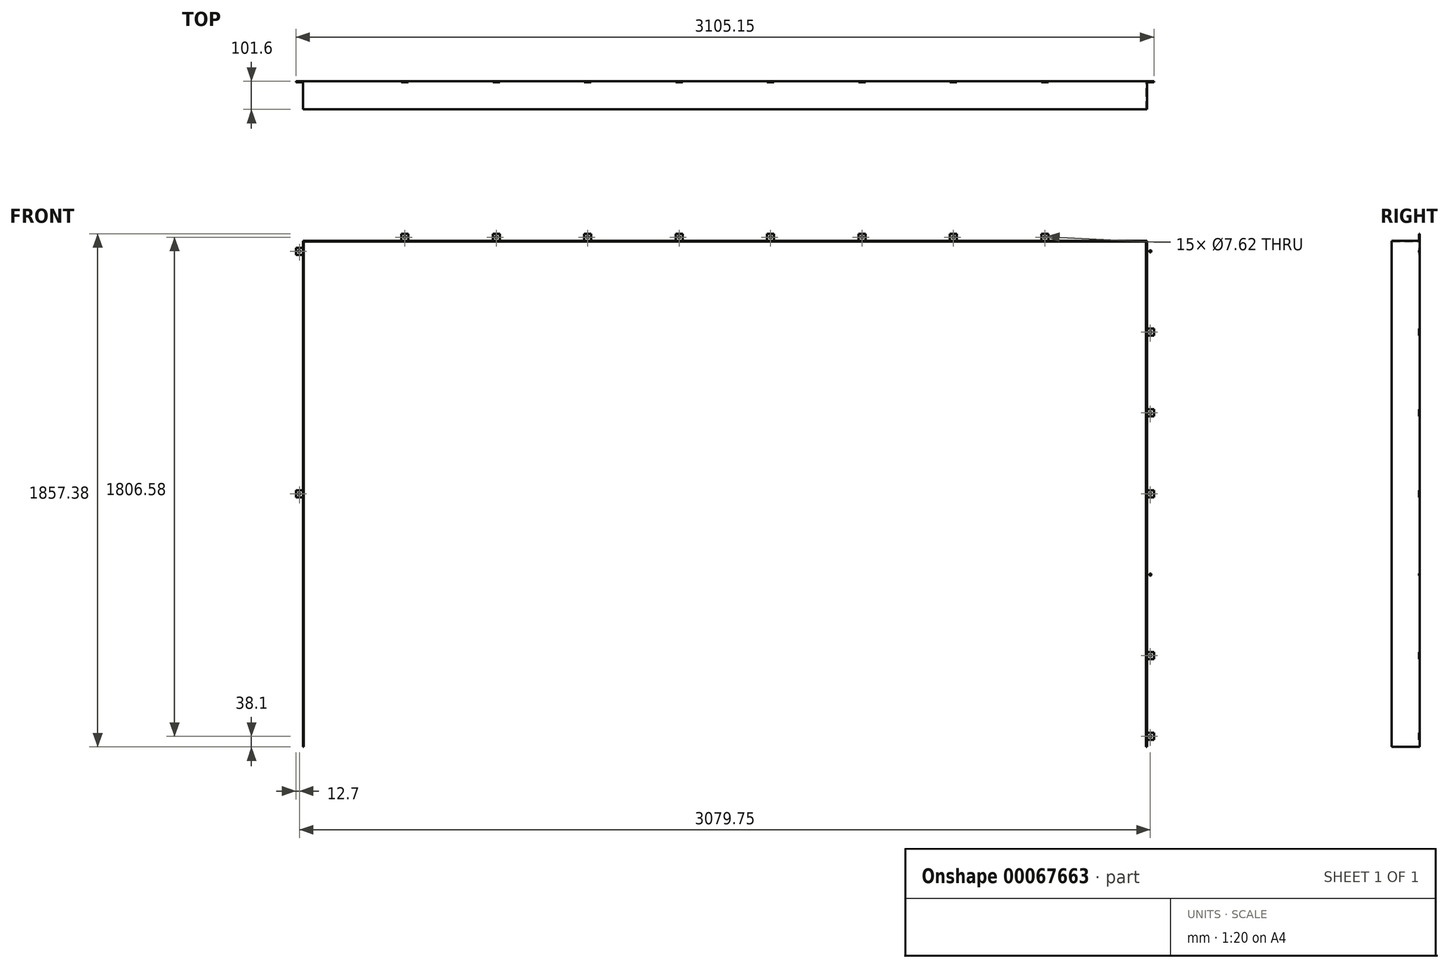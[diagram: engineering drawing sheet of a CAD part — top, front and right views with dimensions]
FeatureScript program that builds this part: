
annotation { "Feature Type Name" : "Feature", "Feature Type Description" : "" }
export const myFeature = defineFeature(function(context is Context, id is Id, definition is map)
    precondition{}
    {
        {
            var Q0;
            Q0=qCreatedBy(makeId("Front.planeOp"),FACE);
            var sketch = newSketch(context, id + "F0", { "sketchPlane" : qUnion([Q0])});
            skLineSegment(sketch, "E0", {"start": v(0, 0) * mm, "end": v(0, 1831.98) * mm});
            skLineSegment(sketch, "E1", {"start": v(0, 1831.98) * mm, "end": v(3054.35, 1831.98) * mm});
            skLineSegment(sketch, "E2", {"start": v(3054.35, 1831.98) * mm, "end": v(3054.35, 0) * mm});
            skLineSegment(sketch, "E3", {"start": v(3054.35, 0) * mm, "end": v(3051.18, 0) * mm});
            skLineSegment(sketch, "E4", {"start": v(3051.18, 0) * mm, "end": v(3051.18, 1828.8) * mm});
            skLineSegment(sketch, "E5", {"start": v(3051.18, 1828.8) * mm, "end": v(3.17, 1828.8) * mm});
            skLineSegment(sketch, "E6", {"start": v(3.18, 1828.8) * mm, "end": v(3.18, 0) * mm});
            skLineSegment(sketch, "E7", {"start": v(3.18, 0) * mm, "end": v(0, 0) * mm});
            skLineSegment(sketch, "E8", {"start": v(1527.18, 1831.98) * mm, "end": v(1527.18, 1828.8) * mm, "construction": true});
            skLineSegment(sketch, "E9", {"start": v(1527.18, 1828.8) * mm, "end": v(1527.18, -376.43) * mm, "construction": true});
            skLineSegment(sketch, "E10.bottom", {"start": v(0, 1806.57) * mm, "end": v(-25.4, 1806.57) * mm});
            skLineSegment(sketch, "E10.top", {"start": v(0, 1781.17) * mm, "end": v(-25.4, 1781.17) * mm});
            skLineSegment(sketch, "E10.left", {"start": v(0, 1806.57) * mm, "end": v(0, 1781.17) * mm});
            skLineSegment(sketch, "E10.right", {"start": v(-25.4, 1806.57) * mm, "end": v(-25.4, 1781.17) * mm});
            skLineSegment(sketch, "E11", {"start": v(-12.7, 1806.57) * mm, "end": v(-12.7, 1781.17) * mm, "construction": true});
            skLineSegment(sketch, "E12", {"start": v(-25.4, 1793.87) * mm, "end": v(0, 1793.87) * mm, "construction": true});
            skCircle(sketch, "E13", {"center": v(-12.7, 1793.87) * mm, "radius": 3.81 * mm});
            skLineSegment(sketch, "E14.left", {"start": v(0, 1513.95) * mm, "end": v(0, 1488.55) * mm});
            skLineSegment(sketch, "E15", {"start": v(-25.4, 1501.25) * mm, "end": v(0, 1501.25) * mm, "construction": true});
            skLineSegment(sketch, "E16", {"start": v(-12.7, 1513.95) * mm, "end": v(-12.7, 1488.55) * mm, "construction": true});
            skLineSegment(sketch, "E14.right", {"start": v(-25.4, 1513.95) * mm, "end": v(-25.4, 1488.55) * mm});
            skLineSegment(sketch, "E14.top", {"start": v(0, 1488.55) * mm, "end": v(-25.4, 1488.55) * mm});
            skLineSegment(sketch, "E14.bottom", {"start": v(0, 1513.95) * mm, "end": v(-25.4, 1513.95) * mm});
            skCircle(sketch, "E17", {"center": v(-12.7, 1501.25) * mm, "radius": 3.81 * mm});
            skLineSegment(sketch, "E18.left", {"start": v(0, 1221.32) * mm, "end": v(0, 1195.92) * mm});
            skLineSegment(sketch, "E19", {"start": v(-25.4, 1208.62) * mm, "end": v(0, 1208.62) * mm, "construction": true});
            skLineSegment(sketch, "E20", {"start": v(-12.7, 1221.32) * mm, "end": v(-12.7, 1195.92) * mm, "construction": true});
            skLineSegment(sketch, "E18.right", {"start": v(-25.4, 1221.32) * mm, "end": v(-25.4, 1195.92) * mm});
            skLineSegment(sketch, "E18.top", {"start": v(0, 1195.92) * mm, "end": v(-25.4, 1195.92) * mm});
            skLineSegment(sketch, "E18.bottom", {"start": v(0, 1221.32) * mm, "end": v(-25.4, 1221.32) * mm});
            skCircle(sketch, "E21", {"center": v(-12.7, 1208.62) * mm, "radius": 3.81 * mm});
            skLineSegment(sketch, "E22.left", {"start": v(0, 50.8) * mm, "end": v(0, 25.4) * mm});
            skLineSegment(sketch, "E23", {"start": v(-25.4, 38.1) * mm, "end": v(0, 38.1) * mm, "construction": true});
            skLineSegment(sketch, "E24", {"start": v(-12.7, 50.8) * mm, "end": v(-12.7, 25.4) * mm, "construction": true});
            skLineSegment(sketch, "E22.right", {"start": v(-25.4, 50.8) * mm, "end": v(-25.4, 25.4) * mm});
            skLineSegment(sketch, "E22.top", {"start": v(0, 25.4) * mm, "end": v(-25.4, 25.4) * mm});
            skLineSegment(sketch, "E22.bottom", {"start": v(0, 50.8) * mm, "end": v(-25.4, 50.8) * mm});
            skCircle(sketch, "E25", {"center": v(-12.7, 38.1) * mm, "radius": 3.81 * mm});
            skLineSegment(sketch, "E26.left", {"start": v(0, 343.43) * mm, "end": v(0, 318.03) * mm});
            skLineSegment(sketch, "E27", {"start": v(-25.4, 330.73) * mm, "end": v(0, 330.73) * mm, "construction": true});
            skLineSegment(sketch, "E28", {"start": v(-12.7, 343.43) * mm, "end": v(-12.7, 318.03) * mm, "construction": true});
            skLineSegment(sketch, "E26.right", {"start": v(-25.4, 343.43) * mm, "end": v(-25.4, 318.03) * mm});
            skLineSegment(sketch, "E26.top", {"start": v(0, 318.03) * mm, "end": v(-25.4, 318.03) * mm});
            skLineSegment(sketch, "E26.bottom", {"start": v(0, 343.43) * mm, "end": v(-25.4, 343.43) * mm});
            skCircle(sketch, "E29", {"center": v(-12.7, 330.73) * mm, "radius": 3.81 * mm});
            skLineSegment(sketch, "E30.left", {"start": v(0, 636.06) * mm, "end": v(0, 610.66) * mm});
            skLineSegment(sketch, "E31", {"start": v(-25.4, 623.36) * mm, "end": v(0, 623.36) * mm, "construction": true});
            skLineSegment(sketch, "E32", {"start": v(-12.7, 636.06) * mm, "end": v(-12.7, 610.66) * mm, "construction": true});
            skLineSegment(sketch, "E30.right", {"start": v(-25.4, 636.06) * mm, "end": v(-25.4, 610.66) * mm});
            skLineSegment(sketch, "E30.top", {"start": v(0, 610.66) * mm, "end": v(-25.4, 610.66) * mm});
            skLineSegment(sketch, "E30.bottom", {"start": v(0, 636.06) * mm, "end": v(-25.4, 636.06) * mm});
            skCircle(sketch, "E33", {"center": v(-12.7, 623.36) * mm, "radius": 3.81 * mm});
            skLineSegment(sketch, "E34.MirrorCS", {"start": v(3079.75, 1793.87) * mm, "end": v(3054.35, 1793.87) * mm, "construction": true});
            skCircle(sketch, "E35.MirrorC", {"center": v(3067.05, 1793.88) * mm, "radius": 3.81 * mm});
            skLineSegment(sketch, "E36.MirrorCS", {"start": v(3054.35, 1806.57) * mm, "end": v(3079.75, 1806.57) * mm});
            skLineSegment(sketch, "E37.MirrorCS", {"start": v(3067.05, 1806.58) * mm, "end": v(3067.05, 1781.18) * mm, "construction": true});
            skLineSegment(sketch, "E38.MirrorCS", {"start": v(3079.75, 1806.58) * mm, "end": v(3079.75, 1781.18) * mm});
            skLineSegment(sketch, "E39.MirrorCS", {"start": v(3054.35, 1806.58) * mm, "end": v(3054.35, 1781.18) * mm});
            skLineSegment(sketch, "E40.MirrorCS", {"start": v(3054.35, 1781.17) * mm, "end": v(3079.75, 1781.17) * mm});
            skLineSegment(sketch, "E41.MirrorCS", {"start": v(3079.75, 1501.25) * mm, "end": v(3054.35, 1501.25) * mm, "construction": true});
            skLineSegment(sketch, "E42.MirrorCS", {"start": v(3054.35, 1513.95) * mm, "end": v(3079.75, 1513.95) * mm});
            skCircle(sketch, "E43.MirrorC", {"center": v(3067.05, 1501.25) * mm, "radius": 3.81 * mm});
            skLineSegment(sketch, "E44.MirrorCS", {"start": v(3054.35, 1513.95) * mm, "end": v(3054.35, 1488.55) * mm});
            skLineSegment(sketch, "E45.MirrorCS", {"start": v(3067.05, 1513.95) * mm, "end": v(3067.05, 1488.55) * mm, "construction": true});
            skLineSegment(sketch, "E46.MirrorCS", {"start": v(3079.75, 1513.95) * mm, "end": v(3079.75, 1488.55) * mm});
            skLineSegment(sketch, "E47.MirrorCS", {"start": v(3054.35, 1488.55) * mm, "end": v(3079.75, 1488.55) * mm});
            skLineSegment(sketch, "E48.MirrorCS", {"start": v(3079.75, 1221.32) * mm, "end": v(3079.75, 1195.92) * mm});
            skLineSegment(sketch, "E49.MirrorCS", {"start": v(3079.75, 1208.62) * mm, "end": v(3054.35, 1208.62) * mm, "construction": true});
            skLineSegment(sketch, "E50.MirrorCS", {"start": v(3067.05, 1221.32) * mm, "end": v(3067.05, 1195.92) * mm, "construction": true});
            skCircle(sketch, "E51.MirrorC", {"center": v(3067.05, 1208.62) * mm, "radius": 3.81 * mm});
            skLineSegment(sketch, "E52.MirrorCS", {"start": v(3054.35, 1195.92) * mm, "end": v(3079.75, 1195.92) * mm});
            skLineSegment(sketch, "E53.MirrorCS", {"start": v(3054.35, 1221.32) * mm, "end": v(3054.35, 1195.92) * mm});
            skLineSegment(sketch, "E54.MirrorCS", {"start": v(3054.35, 1221.32) * mm, "end": v(3079.75, 1221.32) * mm});
            skCircle(sketch, "E55.MirrorC", {"center": v(3067.05, 623.36) * mm, "radius": 3.81 * mm});
            skLineSegment(sketch, "E56.MirrorCS", {"start": v(3054.35, 636.06) * mm, "end": v(3079.75, 636.06) * mm});
            skLineSegment(sketch, "E57.MirrorCS", {"start": v(3079.75, 623.36) * mm, "end": v(3054.35, 623.36) * mm, "construction": true});
            skLineSegment(sketch, "E58.MirrorCS", {"start": v(3067.05, 636.06) * mm, "end": v(3067.05, 610.66) * mm, "construction": true});
            skLineSegment(sketch, "E59.MirrorCS", {"start": v(3054.35, 636.06) * mm, "end": v(3054.35, 610.66) * mm});
            skLineSegment(sketch, "E60.MirrorCS", {"start": v(3054.35, 610.66) * mm, "end": v(3079.75, 610.66) * mm});
            skLineSegment(sketch, "E61.MirrorCS", {"start": v(3079.75, 636.06) * mm, "end": v(3079.75, 610.66) * mm});
            skLineSegment(sketch, "E62.MirrorCS", {"start": v(3079.75, 343.43) * mm, "end": v(3079.75, 318.03) * mm});
            skLineSegment(sketch, "E63.MirrorCS", {"start": v(3054.35, 318.03) * mm, "end": v(3079.75, 318.03) * mm});
            skLineSegment(sketch, "E64.MirrorCS", {"start": v(3067.05, 343.43) * mm, "end": v(3067.05, 318.03) * mm, "construction": true});
            skLineSegment(sketch, "E65.MirrorCS", {"start": v(3054.35, 343.43) * mm, "end": v(3079.75, 343.43) * mm});
            skLineSegment(sketch, "E66.MirrorCS", {"start": v(3079.75, 330.73) * mm, "end": v(3054.35, 330.73) * mm, "construction": true});
            skLineSegment(sketch, "E67.MirrorCS", {"start": v(3054.35, 343.43) * mm, "end": v(3054.35, 318.03) * mm});
            skCircle(sketch, "E68.MirrorC", {"center": v(3067.05, 330.73) * mm, "radius": 3.81 * mm});
            skLineSegment(sketch, "E69.MirrorCS", {"start": v(3079.75, 50.8) * mm, "end": v(3079.75, 25.4) * mm});
            skLineSegment(sketch, "E70.MirrorCS", {"start": v(3067.05, 50.8) * mm, "end": v(3067.05, 25.4) * mm, "construction": true});
            skLineSegment(sketch, "E71.MirrorCS", {"start": v(3079.75, 38.1) * mm, "end": v(3054.35, 38.1) * mm, "construction": true});
            skCircle(sketch, "E72.MirrorC", {"center": v(3067.05, 38.1) * mm, "radius": 3.81 * mm});
            skLineSegment(sketch, "E73.MirrorCS", {"start": v(3054.35, 50.8) * mm, "end": v(3079.75, 50.8) * mm});
            skLineSegment(sketch, "E74.MirrorCS", {"start": v(3054.35, 50.8) * mm, "end": v(3054.35, 25.4) * mm});
            skLineSegment(sketch, "E75.MirrorCS", {"start": v(3054.35, 25.4) * mm, "end": v(3079.75, 25.4) * mm});
            skLineSegment(sketch, "E76.bottom", {"start": v(25.4, 1831.98) * mm, "end": v(50.8, 1831.98) * mm});
            skLineSegment(sketch, "E76.top", {"start": v(25.4, 1857.38) * mm, "end": v(50.8, 1857.38) * mm});
            skLineSegment(sketch, "E76.left", {"start": v(25.4, 1831.98) * mm, "end": v(25.4, 1857.38) * mm});
            skLineSegment(sketch, "E76.right", {"start": v(50.8, 1831.98) * mm, "end": v(50.8, 1857.38) * mm});
            skLineSegment(sketch, "E77.bottom", {"start": v(3028.95, 1831.98) * mm, "end": v(3003.55, 1831.98) * mm});
            skLineSegment(sketch, "E77.top", {"start": v(3028.95, 1857.38) * mm, "end": v(3003.55, 1857.38) * mm});
            skLineSegment(sketch, "E77.left", {"start": v(3028.95, 1831.98) * mm, "end": v(3028.95, 1857.38) * mm});
            skLineSegment(sketch, "E77.right", {"start": v(3003.55, 1831.98) * mm, "end": v(3003.55, 1857.38) * mm});
            skLineSegment(sketch, "E78", {"start": v(3003.55, 1857.38) * mm, "end": v(3028.95, 1831.97) * mm, "construction": true});
            skLineSegment(sketch, "E79", {"start": v(3028.95, 1857.37) * mm, "end": v(3003.55, 1831.97) * mm, "construction": true});
            skCircle(sketch, "E80", {"center": v(3016.25, 1844.68) * mm, "radius": 3.81 * mm});
            skLineSegment(sketch, "E81", {"start": v(25.4, 1857.38) * mm, "end": v(50.8, 1831.98) * mm, "construction": true});
            skLineSegment(sketch, "E82", {"start": v(50.8, 1857.38) * mm, "end": v(25.4, 1831.98) * mm, "construction": true});
            skCircle(sketch, "E83", {"center": v(38.1, 1844.68) * mm, "radius": 3.81 * mm});
            skLineSegment(sketch, "E84", {"start": v(356.3, 1844.68) * mm, "end": v(381.7, 1844.68) * mm, "construction": true});
            skCircle(sketch, "E85", {"center": v(369, 1844.68) * mm, "radius": 3.81 * mm});
            skLineSegment(sketch, "E86.left", {"start": v(381.7, 1857.38) * mm, "end": v(381.7, 1831.98) * mm});
            skLineSegment(sketch, "E86.top", {"start": v(381.7, 1831.98) * mm, "end": v(356.3, 1831.98) * mm});
            skLineSegment(sketch, "E86.bottom", {"start": v(381.7, 1857.38) * mm, "end": v(356.3, 1857.38) * mm});
            skLineSegment(sketch, "E87", {"start": v(369, 1857.38) * mm, "end": v(369, 1831.98) * mm, "construction": true});
            skLineSegment(sketch, "E86.right", {"start": v(356.3, 1857.38) * mm, "end": v(356.3, 1831.97) * mm});
            skLineSegment(sketch, "E88", {"start": v(1349.02, 1844.68) * mm, "end": v(1374.42, 1844.68) * mm, "construction": true});
            skCircle(sketch, "E89", {"center": v(1361.72, 1844.68) * mm, "radius": 3.81 * mm});
            skLineSegment(sketch, "E90.left", {"start": v(1374.42, 1857.38) * mm, "end": v(1374.42, 1831.98) * mm});
            skLineSegment(sketch, "E90.top", {"start": v(1374.42, 1831.98) * mm, "end": v(1349.02, 1831.98) * mm});
            skLineSegment(sketch, "E90.bottom", {"start": v(1374.42, 1857.38) * mm, "end": v(1349.02, 1857.38) * mm});
            skLineSegment(sketch, "E91", {"start": v(1361.72, 1857.38) * mm, "end": v(1361.72, 1831.98) * mm, "construction": true});
            skLineSegment(sketch, "E90.right", {"start": v(1349.02, 1857.38) * mm, "end": v(1349.02, 1831.98) * mm});
            skLineSegment(sketch, "E92", {"start": v(2341.74, 1844.68) * mm, "end": v(2367.14, 1844.68) * mm, "construction": true});
            skCircle(sketch, "E93", {"center": v(2354.44, 1844.68) * mm, "radius": 3.81 * mm});
            skLineSegment(sketch, "E94.left", {"start": v(2367.14, 1857.38) * mm, "end": v(2367.14, 1831.98) * mm});
            skLineSegment(sketch, "E94.top", {"start": v(2367.14, 1831.98) * mm, "end": v(2341.74, 1831.98) * mm});
            skLineSegment(sketch, "E94.bottom", {"start": v(2367.14, 1857.38) * mm, "end": v(2341.74, 1857.38) * mm});
            skLineSegment(sketch, "E95", {"start": v(2354.44, 1857.38) * mm, "end": v(2354.44, 1831.98) * mm, "construction": true});
            skLineSegment(sketch, "E94.right", {"start": v(2341.74, 1857.38) * mm, "end": v(2341.74, 1831.97) * mm});
            skLineSegment(sketch, "E96.top", {"start": v(0, 903.29) * mm, "end": v(-25.4, 903.29) * mm});
            skLineSegment(sketch, "E97", {"start": v(-12.7, 928.69) * mm, "end": v(-12.7, 903.29) * mm, "construction": true});
            skCircle(sketch, "E98", {"center": v(-12.7, 915.99) * mm, "radius": 3.81 * mm});
            skLineSegment(sketch, "E99", {"start": v(-25.4, 915.99) * mm, "end": v(0, 915.99) * mm, "construction": true});
            skLineSegment(sketch, "E96.left", {"start": v(0, 928.69) * mm, "end": v(0, 903.29) * mm});
            skLineSegment(sketch, "E96.bottom", {"start": v(0, 928.69) * mm, "end": v(-25.4, 928.69) * mm});
            skLineSegment(sketch, "E96.right", {"start": v(-25.4, 928.69) * mm, "end": v(-25.4, 903.29) * mm});
            skLineSegment(sketch, "E100", {"start": v(-12.7, 38.1) * mm, "end": v(-12.7, 330.73) * mm, "construction": true});
            skLineSegment(sketch, "E101", {"start": v(-12.7, 330.73) * mm, "end": v(-12.7, 623.36) * mm, "construction": true});
            skLineSegment(sketch, "E102", {"start": v(-12.7, 623.36) * mm, "end": v(-12.7, 915.99) * mm, "construction": true});
            skLineSegment(sketch, "E103", {"start": v(-12.7, 915.99) * mm, "end": v(-12.7, 1208.62) * mm, "construction": true});
            skLineSegment(sketch, "E104", {"start": v(-12.7, 1208.62) * mm, "end": v(-12.7, 1501.25) * mm, "construction": true});
            skLineSegment(sketch, "E105", {"start": v(-12.7, 1793.87) * mm, "end": v(-12.7, 1501.25) * mm, "construction": true});
            skLineSegment(sketch, "E106.MirrorCS", {"start": v(3067.05, 928.69) * mm, "end": v(3067.05, 903.29) * mm, "construction": true});
            skLineSegment(sketch, "E107.MirrorCS", {"start": v(3079.75, 915.99) * mm, "end": v(3054.35, 915.99) * mm, "construction": true});
            skLineSegment(sketch, "E108.MirrorCS", {"start": v(3054.35, 928.69) * mm, "end": v(3079.75, 928.69) * mm});
            skCircle(sketch, "E109.MirrorC", {"center": v(3067.05, 915.99) * mm, "radius": 3.81 * mm});
            skLineSegment(sketch, "E110.MirrorCS", {"start": v(3054.35, 903.29) * mm, "end": v(3079.75, 903.29) * mm});
            skLineSegment(sketch, "E111.MirrorCS", {"start": v(3079.75, 928.69) * mm, "end": v(3079.75, 903.29) * mm});
            skLineSegment(sketch, "E112.MirrorCS", {"start": v(3054.35, 928.69) * mm, "end": v(3054.35, 903.29) * mm});
            skLineSegment(sketch, "E113.left", {"start": v(1043.52, 1857.38) * mm, "end": v(1043.52, 1831.98) * mm});
            skLineSegment(sketch, "E113.top", {"start": v(1043.52, 1831.98) * mm, "end": v(1018.12, 1831.98) * mm});
            skLineSegment(sketch, "E114", {"start": v(1030.82, 1857.38) * mm, "end": v(1030.82, 1831.98) * mm, "construction": true});
            skCircle(sketch, "E115", {"center": v(1030.82, 1844.68) * mm, "radius": 3.81 * mm});
            skLineSegment(sketch, "E113.bottom", {"start": v(1043.52, 1857.38) * mm, "end": v(1018.12, 1857.38) * mm});
            skLineSegment(sketch, "E116", {"start": v(1018.12, 1844.67) * mm, "end": v(1043.52, 1844.67) * mm, "construction": true});
            skLineSegment(sketch, "E113.right", {"start": v(1018.12, 1857.38) * mm, "end": v(1018.12, 1831.98) * mm});
            skLineSegment(sketch, "E117.left", {"start": v(2036.23, 1857.38) * mm, "end": v(2036.23, 1831.98) * mm});
            skLineSegment(sketch, "E117.top", {"start": v(2036.23, 1831.98) * mm, "end": v(2010.83, 1831.98) * mm});
            skLineSegment(sketch, "E118", {"start": v(2023.53, 1857.38) * mm, "end": v(2023.53, 1831.98) * mm, "construction": true});
            skCircle(sketch, "E119", {"center": v(2023.53, 1844.68) * mm, "radius": 3.81 * mm});
            skLineSegment(sketch, "E117.bottom", {"start": v(2036.23, 1857.38) * mm, "end": v(2010.83, 1857.38) * mm});
            skLineSegment(sketch, "E120", {"start": v(2010.83, 1844.68) * mm, "end": v(2036.23, 1844.68) * mm, "construction": true});
            skLineSegment(sketch, "E117.right", {"start": v(2010.83, 1857.38) * mm, "end": v(2010.83, 1831.98) * mm});
            skLineSegment(sketch, "E121.left", {"start": v(712.61, 1857.38) * mm, "end": v(712.61, 1831.98) * mm});
            skLineSegment(sketch, "E121.top", {"start": v(712.61, 1831.98) * mm, "end": v(687.21, 1831.98) * mm});
            skLineSegment(sketch, "E122", {"start": v(699.91, 1857.38) * mm, "end": v(699.91, 1831.98) * mm, "construction": true});
            skCircle(sketch, "E123", {"center": v(699.91, 1844.68) * mm, "radius": 3.81 * mm});
            skLineSegment(sketch, "E121.bottom", {"start": v(712.61, 1857.38) * mm, "end": v(687.21, 1857.38) * mm});
            skLineSegment(sketch, "E124", {"start": v(687.21, 1844.68) * mm, "end": v(712.61, 1844.68) * mm, "construction": true});
            skLineSegment(sketch, "E121.right", {"start": v(687.21, 1857.38) * mm, "end": v(687.21, 1831.98) * mm});
            skLineSegment(sketch, "E125.left", {"start": v(2698.04, 1857.38) * mm, "end": v(2698.04, 1831.98) * mm});
            skLineSegment(sketch, "E125.top", {"start": v(2698.04, 1831.98) * mm, "end": v(2672.64, 1831.98) * mm});
            skLineSegment(sketch, "E126", {"start": v(2685.34, 1857.38) * mm, "end": v(2685.34, 1831.98) * mm, "construction": true});
            skCircle(sketch, "E127", {"center": v(2685.34, 1844.68) * mm, "radius": 3.81 * mm});
            skLineSegment(sketch, "E125.bottom", {"start": v(2698.04, 1857.38) * mm, "end": v(2672.64, 1857.38) * mm});
            skLineSegment(sketch, "E128", {"start": v(2672.64, 1844.68) * mm, "end": v(2698.04, 1844.68) * mm, "construction": true});
            skLineSegment(sketch, "E125.right", {"start": v(2672.64, 1857.38) * mm, "end": v(2672.64, 1831.98) * mm});
            skLineSegment(sketch, "E129.left", {"start": v(1705.33, 1857.38) * mm, "end": v(1705.33, 1831.98) * mm});
            skLineSegment(sketch, "E129.top", {"start": v(1705.33, 1831.97) * mm, "end": v(1679.93, 1831.97) * mm});
            skLineSegment(sketch, "E130", {"start": v(1692.63, 1857.38) * mm, "end": v(1692.63, 1831.98) * mm, "construction": true});
            skCircle(sketch, "E131", {"center": v(1692.63, 1844.68) * mm, "radius": 3.81 * mm});
            skLineSegment(sketch, "E129.bottom", {"start": v(1705.33, 1857.38) * mm, "end": v(1679.93, 1857.38) * mm});
            skLineSegment(sketch, "E132", {"start": v(1679.93, 1844.68) * mm, "end": v(1705.33, 1844.68) * mm, "construction": true});
            skLineSegment(sketch, "E129.right", {"start": v(1679.93, 1857.38) * mm, "end": v(1679.93, 1831.98) * mm});
            skLineSegment(sketch, "E133", {"start": v(38.1, 1844.68) * mm, "end": v(369, 1844.68) * mm, "construction": true});
            skLineSegment(sketch, "E134", {"start": v(369, 1844.68) * mm, "end": v(699.91, 1844.68) * mm, "construction": true});
            skLineSegment(sketch, "E135", {"start": v(699.91, 1844.68) * mm, "end": v(1030.82, 1844.68) * mm, "construction": true});
            skLineSegment(sketch, "E136", {"start": v(1030.82, 1844.67) * mm, "end": v(1361.72, 1844.67) * mm, "construction": true});
            skLineSegment(sketch, "E137", {"start": v(1361.72, 1844.68) * mm, "end": v(1692.63, 1844.68) * mm, "construction": true});
            skLineSegment(sketch, "E138", {"start": v(1692.63, 1844.68) * mm, "end": v(2023.53, 1844.68) * mm, "construction": true});
            skLineSegment(sketch, "E139", {"start": v(2023.53, 1844.68) * mm, "end": v(2354.44, 1844.68) * mm, "construction": true});
            skLineSegment(sketch, "E140", {"start": v(2354.44, 1844.68) * mm, "end": v(2685.34, 1844.68) * mm, "construction": true});
            skLineSegment(sketch, "E141", {"start": v(2685.34, 1844.68) * mm, "end": v(3016.25, 1844.68) * mm, "construction": true});
            skSolve(sketch);
        }
        {
            var Q0;
            {var subQ15=sQuery(id+"F0.wireOp",EDGE,"E1");Q0=makeQuery(id+"F0.imprint","IMPRINT",FACE,{"disambiguationData":[TD([[makeQuery(id+"F0.imprint","IMPRINT",EDGE,{"derivedFrom":subQ15}),-1.0]])]});}
            extrude(context, id + "F1", {"entities" : qUnion([Q0]), "depth" : 101.6 * mm});
        }
        {
            var Q0;
            Q0=makeQuery(id+"F0.imprint","IMPRINT",FACE,{"disambiguationData":[TD([[makeQuery(id+"F0.imprint","IMPRINT",EDGE,{"derivedFrom":sQuery(id+"F0.wireOp",EDGE,"E69.MirrorCS")}),-1.0]])]});
            var Q1;
            Q1=makeQuery(id+"F0.imprint","IMPRINT",FACE,{"disambiguationData":[TD([[makeQuery(id+"F0.imprint","IMPRINT",EDGE,{"derivedFrom":sQuery(id+"F0.wireOp",EDGE,"E62.MirrorCS")}),-1.0]])]});
            var Q2;
            Q2=makeQuery(id+"F0.imprint","IMPRINT",FACE,{"disambiguationData":[TD([[makeQuery(id+"F0.imprint","IMPRINT",EDGE,{"derivedFrom":sQuery(id+"F0.wireOp",EDGE,"E55.MirrorC")}),1.0]])]});
            var Q3;
            Q3=makeQuery(id+"F0.imprint","IMPRINT",FACE,{"disambiguationData":[TD([[makeQuery(id+"F0.imprint","IMPRINT",EDGE,{"derivedFrom":sQuery(id+"F0.wireOp",EDGE,"E48.MirrorCS")}),-1.0]])]});
            var Q4;
            Q4=makeQuery(id+"F0.imprint","IMPRINT",FACE,{"disambiguationData":[TD([[makeQuery(id+"F0.imprint","IMPRINT",EDGE,{"derivedFrom":sQuery(id+"F0.wireOp",EDGE,"E42.MirrorCS")}),-1.0]])]});
            var Q5;
            Q5=makeQuery(id+"F0.imprint","IMPRINT",FACE,{"disambiguationData":[TD([[makeQuery(id+"F0.imprint","IMPRINT",EDGE,{"derivedFrom":sQuery(id+"F0.wireOp",EDGE,"E35.MirrorC")}),1.0]])]});
            var Q6;
            Q6=makeQuery(id+"F0.imprint","IMPRINT",FACE,{"disambiguationData":[TD([[makeQuery(id+"F0.imprint","IMPRINT",EDGE,{"derivedFrom":sQuery(id+"F0.wireOp",EDGE,"E10.bottom")}),1.0]])]});
            var Q7;
            Q7=makeQuery(id+"F0.imprint","IMPRINT",FACE,{"disambiguationData":[TD([[makeQuery(id+"F0.imprint","IMPRINT",EDGE,{"derivedFrom":sQuery(id+"F0.wireOp",EDGE,"E14.left")}),-1.0]])]});
            var Q8;
            Q8=makeQuery(id+"F0.imprint","IMPRINT",FACE,{"disambiguationData":[TD([[makeQuery(id+"F0.imprint","IMPRINT",EDGE,{"derivedFrom":sQuery(id+"F0.wireOp",EDGE,"E18.left")}),-1.0]])]});
            var Q9;
            Q9=makeQuery(id+"F0.imprint","IMPRINT",FACE,{"disambiguationData":[TD([[makeQuery(id+"F0.imprint","IMPRINT",EDGE,{"derivedFrom":sQuery(id+"F0.wireOp",EDGE,"E30.left")}),-1.0]])]});
            var Q10;
            Q10=makeQuery(id+"F0.imprint","IMPRINT",FACE,{"disambiguationData":[TD([[makeQuery(id+"F0.imprint","IMPRINT",EDGE,{"derivedFrom":sQuery(id+"F0.wireOp",EDGE,"E26.left")}),-1.0]])]});
            var Q11;
            Q11=makeQuery(id+"F0.imprint","IMPRINT",FACE,{"disambiguationData":[TD([[makeQuery(id+"F0.imprint","IMPRINT",EDGE,{"derivedFrom":sQuery(id+"F0.wireOp",EDGE,"E22.left")}),-1.0]])]});
            var Q12;
            Q12=makeQuery(id+"F0.imprint","IMPRINT",FACE,{"disambiguationData":[TD([[makeQuery(id+"F0.imprint","IMPRINT",EDGE,{"derivedFrom":sQuery(id+"F0.wireOp",EDGE,"E76.bottom")}),1.0]])]});
            var Q13;
            Q13=makeQuery(id+"F0.imprint","IMPRINT",FACE,{"disambiguationData":[TD([[makeQuery(id+"F0.imprint","IMPRINT",EDGE,{"derivedFrom":sQuery(id+"F0.wireOp",EDGE,"e8b36b14-baf5-47ac-a38b-4cfdd02c8466.bottom")}),1.0]])]});
            var Q14;
            Q14=makeQuery(id+"F0.imprint","IMPRINT",FACE,{"disambiguationData":[TD([[makeQuery(id+"F0.imprint","IMPRINT",EDGE,{"derivedFrom":sQuery(id+"F0.wireOp",EDGE,"E77.bottom")}),-1.0]])]});
            var Q15;
            Q15=makeQuery(id+"F0.imprint","IMPRINT",FACE,{"disambiguationData":[TD([[makeQuery(id+"F0.imprint","IMPRINT",EDGE,{"derivedFrom":sQuery(id+"F0.wireOp",EDGE,"E85")}),-1.0]])]});
            var Q16;
            Q16=makeQuery(id+"F0.imprint","IMPRINT",FACE,{"disambiguationData":[TD([[makeQuery(id+"F0.imprint","IMPRINT",EDGE,{"derivedFrom":sQuery(id+"F0.wireOp",EDGE,"70c7b6a7-01ed-414b-a764-cb33e45972b0")}),-1.0]])]});
            var Q17;
            Q17=makeQuery(id+"F0.imprint","IMPRINT",FACE,{"disambiguationData":[TD([[makeQuery(id+"F0.imprint","IMPRINT",EDGE,{"derivedFrom":sQuery(id+"F0.wireOp",EDGE,"E89")}),-1.0]])]});
            var Q18;
            Q18=makeQuery(id+"F0.imprint","IMPRINT",FACE,{"disambiguationData":[TD([[makeQuery(id+"F0.imprint","IMPRINT",EDGE,{"derivedFrom":sQuery(id+"F0.wireOp",EDGE,"E93")}),-1.0]])]});
            var Q19;
            Q19=makeQuery(id+"F0.imprint","IMPRINT",FACE,{"disambiguationData":[TD([[makeQuery(id+"F0.imprint","IMPRINT",EDGE,{"derivedFrom":sQuery(id+"F0.wireOp",EDGE,"E96.top")}),-1.0]])]});
            var Q20;
            Q20=makeQuery(id+"F0.imprint","IMPRINT",FACE,{"disambiguationData":[TD([[makeQuery(id+"F0.imprint","IMPRINT",EDGE,{"derivedFrom":sQuery(id+"F0.wireOp",EDGE,"E110.MirrorCS")}),1.0]])]});
            var Q21;
            Q21=makeQuery(id+"F0.imprint","IMPRINT",FACE,{"disambiguationData":[TD([[makeQuery(id+"F0.imprint","IMPRINT",EDGE,{"derivedFrom":sQuery(id+"F0.wireOp",EDGE,"E121.left")}),-1.0]])]});
            var Q22;
            Q22=makeQuery(id+"F0.imprint","IMPRINT",FACE,{"disambiguationData":[TD([[makeQuery(id+"F0.imprint","IMPRINT",EDGE,{"derivedFrom":sQuery(id+"F0.wireOp",EDGE,"E113.left")}),-1.0]])]});
            var Q23;
            Q23=makeQuery(id+"F0.imprint","IMPRINT",FACE,{"disambiguationData":[TD([[makeQuery(id+"F0.imprint","IMPRINT",EDGE,{"derivedFrom":sQuery(id+"F0.wireOp",EDGE,"E129.left")}),-1.0]])]});
            var Q24;
            Q24=makeQuery(id+"F0.imprint","IMPRINT",FACE,{"disambiguationData":[TD([[makeQuery(id+"F0.imprint","IMPRINT",EDGE,{"derivedFrom":sQuery(id+"F0.wireOp",EDGE,"E117.left")}),-1.0]])]});
            var Q25;
            Q25=makeQuery(id+"F0.imprint","IMPRINT",FACE,{"disambiguationData":[TD([[makeQuery(id+"F0.imprint","IMPRINT",EDGE,{"derivedFrom":sQuery(id+"F0.wireOp",EDGE,"E125.left")}),-1.0]])]});
            extrude(context, id + "F2", {"entities" : qUnion([Q0, Q1, Q2, Q3, Q4, Q5, Q6, Q7, Q8, Q9, Q10, Q11, Q12, Q13, Q14, Q15, Q16, Q17, Q18, Q19, Q20, Q21, Q22, Q23, Q24, Q25]), "operationType" : NewBodyOperationType.ADD, "depth" : 3.17 * mm});
        }
    });
